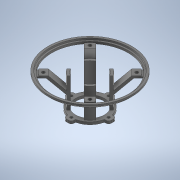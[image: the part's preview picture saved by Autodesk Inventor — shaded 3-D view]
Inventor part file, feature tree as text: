
AUTODESK INVENTOR PART (.ipt)
format: ipt  version: 2020 (Build 240168000, 168)  size: 484,864 bytes
history: native  units: mm
features: projected_geometry x23, sketch x14, extrude x7, other x4, pattern_circular x1, sweep x1
ambient origin geometry x8: Origin, YZ Plane, XZ Plane, XY Plane, X Axis, Y Axis, Z Axis, Center Point
bodies: Body1 (feature_tree)
feature tree (50):
  other  "Твердое тело1"
  extrude  "Выдавливание1"  Depth=44.0mm
  extrude  "Выдавливание2"  Depth=3.0mm
  sketch  "Эскиз3"
  extrude  "Выдавливание4"  Depth=40.0mm TaperAngle=360.0deg
  pattern_circular  "Круговой массив1"  [2 undecoded]
  other  "РабПлоскость2"
  sketch  "Эскиз5"
  other  "РабПлоскость1"
  sketch  "Эскиз6"
  sketch  "Эскиз7"
  extrude  "Выдавливание6"  Depth=4.5mm
  sketch  "Эскиз8"
  extrude  "Выдавливание7"  Depth=3.0mm
  sketch  "Эскиз9"
  other  "РабПлоскость3"
  sketch  "Эскиз10"
  sweep  "Сдвиг1"
  extrude  "Выдавливание8"  Depth=1.0mm
  extrude  "Выдавливание9"  TaperAngle=45.0deg  [1 undecoded]
  sketch  "Эскиз1"
  sketch  "Эскиз2"
  sketch  "Эскиз4"
  projected_geometry  "Спроецированная петля1"
  projected_geometry  "Спроецированная петля2"
  projected_geometry  "Спроецированная петля3"
  projected_geometry  "Спроецированная петля4"
  projected_geometry  "Спроецированная петля5"
  projected_geometry  "Спроецированная петля6"
  projected_geometry  "Спроецированная петля7"
  projected_geometry  "Спроецированная петля8"
  projected_geometry  "Спроецированная петля9"
  projected_geometry  "Спроецированная петля10"
  projected_geometry  "Спроецированная петля11"
  projected_geometry  "Спроецированная петля12"
  projected_geometry  "Спроецированная петля13"
  projected_geometry  "Спроецированная петля14"
  projected_geometry  "Спроецированная петля15"
  projected_geometry  "Спроецированная петля16"
  projected_geometry  "Спроецированная петля17"
  projected_geometry  "Спроецированная петля18"
  projected_geometry  "Спроецированная петля19"
  projected_geometry  "Спроецированная петля20"
  sketch  "Эскиз11"
  projected_geometry  "Спроецированная петля21"
  projected_geometry  "Спроецированная петля22"
  projected_geometry  "Спроецированная петля23"
  sketch  "3D эскиз1"
  sketch  "Эскиз12"
  sketch  "Эскиз13"
note: 3 required parameter values undecoded (feature->parameter linkage not recoverable at this tier; creation-order binding heuristic only, values carry confidence <= 0.55)
